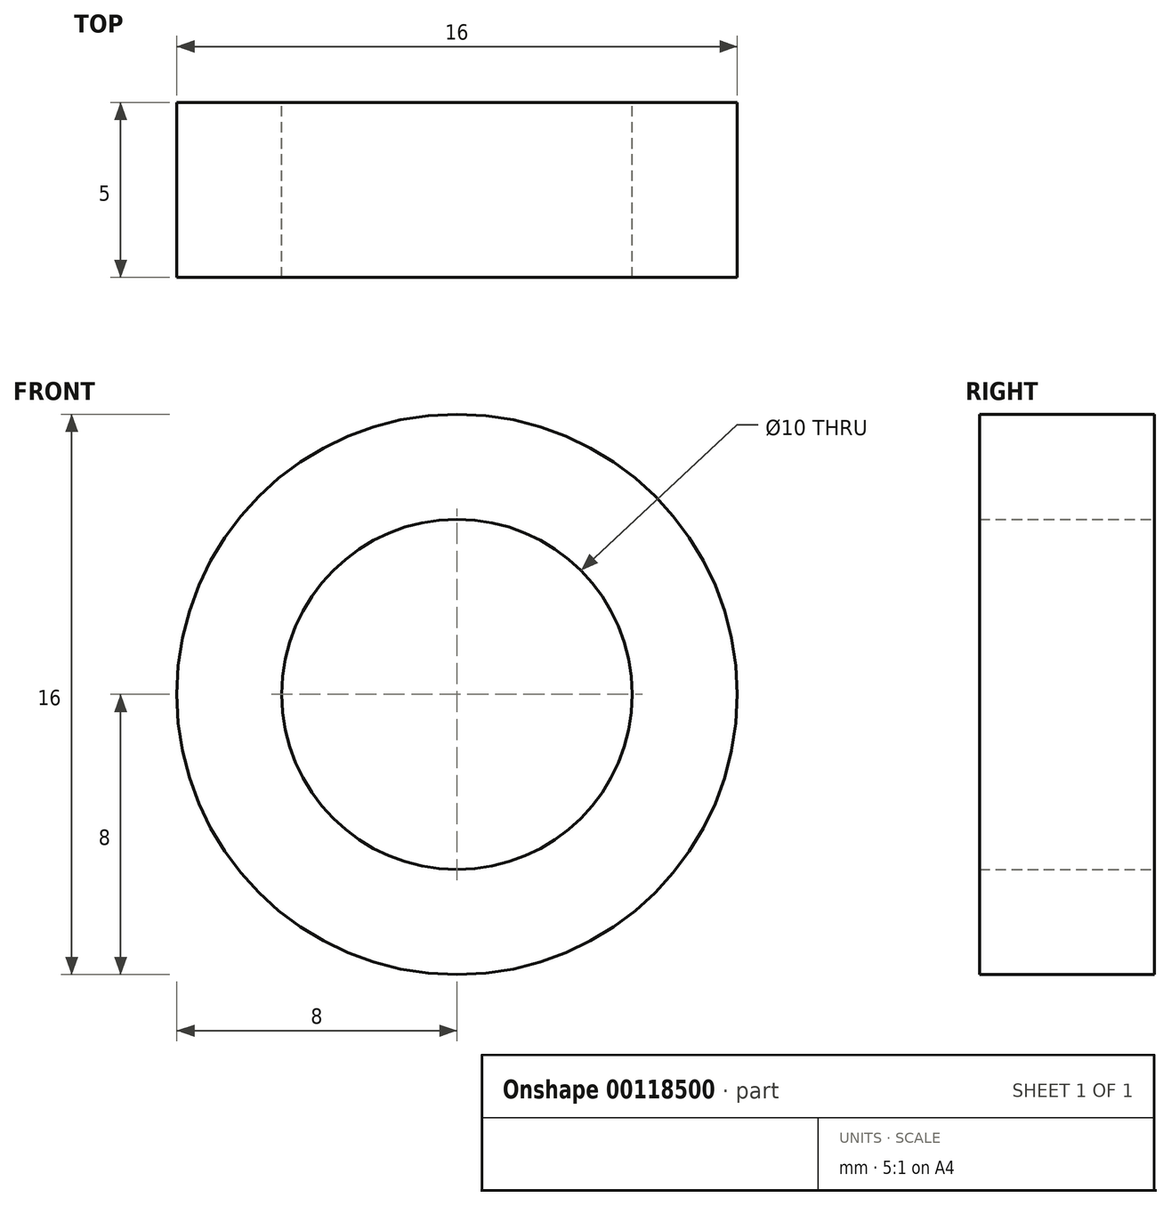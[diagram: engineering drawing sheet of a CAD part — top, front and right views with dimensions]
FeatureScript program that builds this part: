
annotation { "Feature Type Name" : "Feature", "Feature Type Description" : "" }
export const myFeature = defineFeature(function(context is Context, id is Id, definition is map)
    precondition{}
    {
        {
            var Q0;
            Q0=qCreatedBy(makeId("Front.planeOp"),FACE);
            var sketch = newSketch(context, id + "F0", { "sketchPlane" : qUnion([Q0])});
            skCircle(sketch, "E0", {"center": v(0, 0) * mm, "radius": 5 * mm});
            skCircle(sketch, "E1", {"center": v(0, 0) * mm, "radius": 8 * mm});
            skSolve(sketch);
        }
        {
            var Q0;
            Q0 = qSketchRegion(id + "F0", true);
            extrude(context, id + "F1", {"entities" : qUnion([Q0]), "depth" : 5 * mm});
        }
    });
